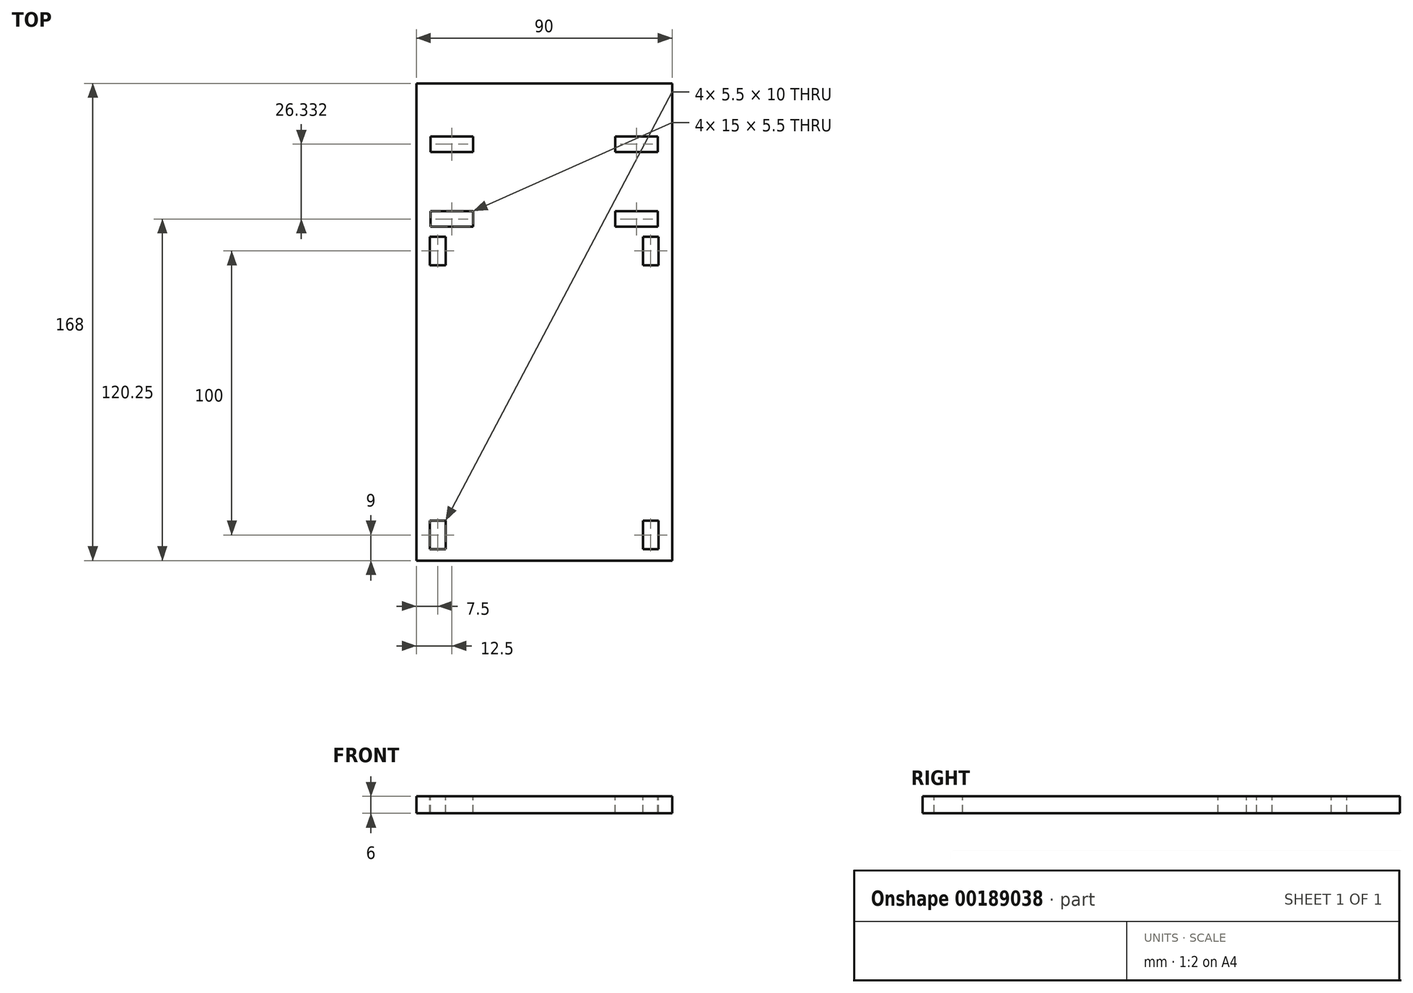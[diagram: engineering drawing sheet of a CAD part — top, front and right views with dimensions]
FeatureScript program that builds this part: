
annotation { "Feature Type Name" : "Feature", "Feature Type Description" : "" }
export const myFeature = defineFeature(function(context is Context, id is Id, definition is map)
    precondition{}
    {
        {
            var Q0;
            Q0=qCreatedBy(makeId("Top.planeOp"),FACE);
            var sketch = newSketch(context, id + "F0", { "sketchPlane" : qUnion([Q0])});
            skLineSegment(sketch, "E0.bottom", {"start": v(45, -59) * mm, "end": v(-45, -59) * mm});
            skLineSegment(sketch, "E0.top", {"start": v(45, 59) * mm, "end": v(-45, 59) * mm});
            skLineSegment(sketch, "E0.left", {"start": v(45, -59) * mm, "end": v(45, 59) * mm});
            skLineSegment(sketch, "E0.right", {"start": v(-45, -59) * mm, "end": v(-45, 59) * mm});
            skPoint(sketch, "E0.middle", {"position": v(0, 0) * mm});
            skSolve(sketch);
        }
        {
            var Q0;
            Q0 = qSketchRegion(id + "F0", true);
            extrude(context, id + "F1", {"entities" : qUnion([Q0]), "depth" : 6 * mm});
        }
        {
            var Q0;
            Q0=makeQuery(id+"F1.opExtrude","CAP_FACE",FACE,{"disambiguationData":[OSD([sQuery(id+"F0.wireOp",EDGE,"E0.bottom"),sQuery(id+"F0.wireOp",EDGE,"E0.top"),sQuery(id+"F0.wireOp",EDGE,"E0.left"),sQuery(id+"F0.wireOp",EDGE,"E0.right")])],"isStart":false});
            var sketch = newSketch(context, id + "F2", { "sketchPlane" : qUnion([Q0])});
            skLineSegment(sketch, "E1.bottom", {"start": v(-45, 59) * mm, "end": v(45, 59) * mm});
            skLineSegment(sketch, "E1.top", {"start": v(-45, 109) * mm, "end": v(45, 109) * mm});
            skLineSegment(sketch, "E1.left", {"start": v(-45, 59) * mm, "end": v(-45, 109) * mm});
            skLineSegment(sketch, "E1.right", {"start": v(45, 59) * mm, "end": v(45, 109) * mm});
            skSolve(sketch);
        }
        {
            var Q0;
            Q0 = qSketchRegion(id + "F2", true);
            extrude(context, id + "F3", {"entities" : qUnion([Q0]), "operationType" : NewBodyOperationType.ADD, "oppositeDirection" : true, "depth" : 6 * mm});
        }
        {
            var Q0;
            Q0=makeQuery(id+"F3.boolean.opBoolean","MERGE",FACE,{"derivedFrom":[makeQuery(id+"F1.opExtrude","CAP_FACE",FACE,{"disambiguationData":[OSD([sQuery(id+"F0.wireOp",EDGE,"E0.bottom"),sQuery(id+"F0.wireOp",EDGE,"E0.top"),sQuery(id+"F0.wireOp",EDGE,"E0.left"),sQuery(id+"F0.wireOp",EDGE,"E0.right")])],"isStart":false}),makeQuery(id+"F3.opExtrude","CAP_FACE",FACE,{"disambiguationData":[OSD([sQuery(id+"F2.wireOp",EDGE,"E1.bottom"),sQuery(id+"F2.wireOp",EDGE,"E1.top"),sQuery(id+"F2.wireOp",EDGE,"E1.left"),sQuery(id+"F2.wireOp",EDGE,"E1.right")])],"isStart":true})]});
            var sketch = newSketch(context, id + "F4", { "sketchPlane" : qUnion([Q0])});
            skLineSegment(sketch, "E2.bottom", {"start": v(37.5, -50) * mm, "end": v(-37.5, -50) * mm, "construction": true});
            skLineSegment(sketch, "E2.top", {"start": v(37.5, 50) * mm, "end": v(-37.5, 50) * mm, "construction": true});
            skLineSegment(sketch, "E2.left", {"start": v(37.5, -50) * mm, "end": v(37.5, 50) * mm, "construction": true});
            skLineSegment(sketch, "E2.right", {"start": v(-37.5, -50) * mm, "end": v(-37.5, 50) * mm, "construction": true});
            skPoint(sketch, "E2.middle", {"position": v(0, 0) * mm});
            skLineSegment(sketch, "E3.bottom", {"start": v(-34.75, 45) * mm, "end": v(-40.25, 45) * mm});
            skLineSegment(sketch, "E3.top", {"start": v(-34.75, 55) * mm, "end": v(-40.25, 55) * mm});
            skLineSegment(sketch, "E3.left", {"start": v(-34.75, 45) * mm, "end": v(-34.75, 55) * mm});
            skLineSegment(sketch, "E3.right", {"start": v(-40.25, 45) * mm, "end": v(-40.25, 55) * mm});
            skPoint(sketch, "E3.middle", {"position": v(-37.5, 50) * mm});
            skLineSegment(sketch, "E4.bottom", {"start": v(40.25, 45) * mm, "end": v(34.75, 45) * mm});
            skLineSegment(sketch, "E4.top", {"start": v(40.25, 55) * mm, "end": v(34.75, 55) * mm});
            skLineSegment(sketch, "E4.left", {"start": v(40.25, 45) * mm, "end": v(40.25, 55) * mm});
            skLineSegment(sketch, "E4.right", {"start": v(34.75, 45) * mm, "end": v(34.75, 55) * mm});
            skPoint(sketch, "E4.middle", {"position": v(37.5, 50) * mm});
            skLineSegment(sketch, "E5.bottom", {"start": v(40.25, -55) * mm, "end": v(34.75, -55) * mm});
            skLineSegment(sketch, "E5.top", {"start": v(40.25, -45) * mm, "end": v(34.75, -45) * mm});
            skLineSegment(sketch, "E5.left", {"start": v(40.25, -55) * mm, "end": v(40.25, -45) * mm});
            skLineSegment(sketch, "E5.right", {"start": v(34.75, -55) * mm, "end": v(34.75, -45) * mm});
            skPoint(sketch, "E5.middle", {"position": v(37.5, -50) * mm});
            skLineSegment(sketch, "E6.bottom", {"start": v(-34.75, -55) * mm, "end": v(-40.25, -55) * mm});
            skLineSegment(sketch, "E6.top", {"start": v(-34.75, -45) * mm, "end": v(-40.25, -45) * mm});
            skLineSegment(sketch, "E6.left", {"start": v(-34.75, -55) * mm, "end": v(-34.75, -45) * mm});
            skLineSegment(sketch, "E6.right", {"start": v(-40.25, -55) * mm, "end": v(-40.25, -45) * mm});
            skPoint(sketch, "E6.middle", {"position": v(-37.5, -50) * mm});
            skSolve(sketch);
        }
        {
            var Q0;
            Q0 = qSketchRegion(id + "F4", true);
            extrude(context, id + "F5", {"entities" : qUnion([Q0]), "operationType" : NewBodyOperationType.REMOVE, "oppositeDirection" : true, "depth" : 6 * mm});
        }
        {
            var Q0;
            Q0=makeQuery(id+"F3.boolean.opBoolean","MERGE",FACE,{"derivedFrom":[makeQuery(id+"F1.opExtrude","CAP_FACE",FACE,{"disambiguationData":[OSD([sQuery(id+"F0.wireOp",EDGE,"E0.bottom"),sQuery(id+"F0.wireOp",EDGE,"E0.top"),sQuery(id+"F0.wireOp",EDGE,"E0.left"),sQuery(id+"F0.wireOp",EDGE,"E0.right")])],"isStart":false}),makeQuery(id+"F3.opExtrude","CAP_FACE",FACE,{"disambiguationData":[OSD([sQuery(id+"F2.wireOp",EDGE,"E1.bottom"),sQuery(id+"F2.wireOp",EDGE,"E1.top"),sQuery(id+"F2.wireOp",EDGE,"E1.left"),sQuery(id+"F2.wireOp",EDGE,"E1.right")])],"isStart":true})]});
            var sketch = newSketch(context, id + "F6", { "sketchPlane" : qUnion([Q0])});
            skLineSegment(sketch, "E7", {"start": v(0, 64) * mm, "end": v(-40, 64) * mm, "construction": true});
            skLineSegment(sketch, "E8", {"start": v(40, 64) * mm, "end": v(0, 64) * mm, "construction": true});
            skLineSegment(sketch, "E9.bottom", {"start": v(-40, 64) * mm, "end": v(-25, 64) * mm});
            skLineSegment(sketch, "E9.top", {"start": v(-40, 58.5) * mm, "end": v(-25, 58.5) * mm});
            skLineSegment(sketch, "E9.left", {"start": v(-40, 64) * mm, "end": v(-40, 58.5) * mm});
            skLineSegment(sketch, "E9.right", {"start": v(-25, 64) * mm, "end": v(-25, 58.5) * mm});
            skLineSegment(sketch, "E10.bottom", {"start": v(40, 64) * mm, "end": v(25, 64) * mm});
            skLineSegment(sketch, "E10.top", {"start": v(40, 58.5) * mm, "end": v(25, 58.5) * mm});
            skLineSegment(sketch, "E10.left", {"start": v(40, 64) * mm, "end": v(40, 58.5) * mm});
            skLineSegment(sketch, "E10.right", {"start": v(25, 64) * mm, "end": v(25, 58.5) * mm});
            skLineSegment(sketch, "E11", {"start": v(0, 64) * mm, "end": v(0, 90.33) * mm, "construction": true});
            skLineSegment(sketch, "E12", {"start": v(0, 90.33) * mm, "end": v(-40, 90.33) * mm, "construction": true});
            skLineSegment(sketch, "E13", {"start": v(40, 90.33) * mm, "end": v(0, 90.33) * mm, "construction": true});
            skLineSegment(sketch, "E14.bottom", {"start": v(-40, 90.33) * mm, "end": v(-25, 90.33) * mm});
            skLineSegment(sketch, "E14.top", {"start": v(-40, 84.83) * mm, "end": v(-25, 84.83) * mm});
            skLineSegment(sketch, "E14.left", {"start": v(-40, 90.33) * mm, "end": v(-40, 84.83) * mm});
            skLineSegment(sketch, "E14.right", {"start": v(-25, 90.33) * mm, "end": v(-25, 84.83) * mm});
            skLineSegment(sketch, "E15.bottom", {"start": v(40, 90.33) * mm, "end": v(25, 90.33) * mm});
            skLineSegment(sketch, "E15.top", {"start": v(40, 84.83) * mm, "end": v(25, 84.83) * mm});
            skLineSegment(sketch, "E15.left", {"start": v(40, 90.33) * mm, "end": v(40, 84.83) * mm});
            skLineSegment(sketch, "E15.right", {"start": v(25, 90.33) * mm, "end": v(25, 84.83) * mm});
            skSolve(sketch);
        }
        {
            var Q0;
            Q0 = qSketchRegion(id + "F6", true);
            extrude(context, id + "F7", {"entities" : qUnion([Q0]), "operationType" : NewBodyOperationType.REMOVE, "oppositeDirection" : true, "depth" : 6 * mm});
        }
    });
